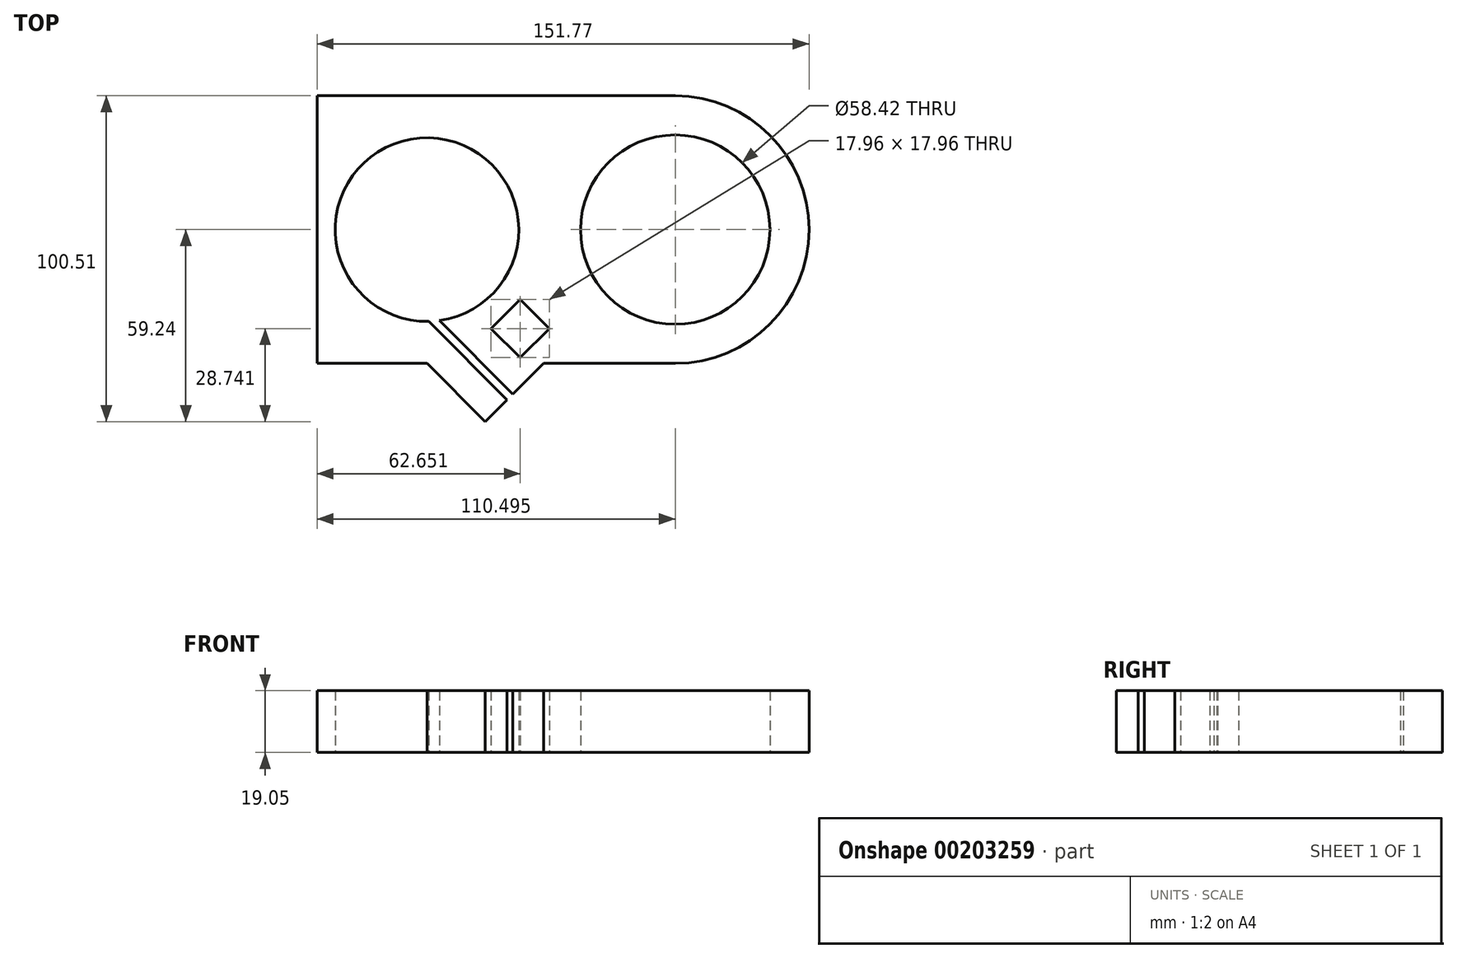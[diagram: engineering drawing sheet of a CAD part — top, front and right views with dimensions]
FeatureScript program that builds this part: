
annotation { "Feature Type Name" : "Feature", "Feature Type Description" : "" }
export const myFeature = defineFeature(function(context is Context, id is Id, definition is map)
    precondition{}
    {
        {
            var Q0;
            Q0=qCreatedBy(makeId("Top.planeOp"),FACE);
            var sketch = newSketch(context, id + "F0", { "sketchPlane" : qUnion([Q0])});
            skLineSegment(sketch, "E0.bottom", {"start": v(55.24, 41.28) * mm, "end": v(-55.25, 41.28) * mm});
            skLineSegment(sketch, "E0.top", {"start": v(55.24, -41.27) * mm, "end": v(14.59, -41.27) * mm});
            skLineSegment(sketch, "E0.right", {"start": v(-55.25, 41.28) * mm, "end": v(-55.25, -41.27) * mm});
            skPoint(sketch, "E0.middle", {"position": v(0, 0) * mm});
            skArc(sketch, "E1", {"start": v(-17.49, -28.06) * mm, "mid": v(-23.52, 28.24) * mm, "end": v(-20.82, -28.32) * mm});
            skArc(sketch, "E2", {"start": v(84.43, 1.27) * mm, "mid": v(26.03, 0) * mm, "end": v(84.43, -1.27) * mm});
            skArc(sketch, "E3", {"start": v(55.24, 41.28) * mm, "mid": v(80.33, 32.78) * mm, "end": v(95.08, 10.8) * mm});
            skArc(sketch, "E4.trimOffspring", {"start": v(95.08, -10.8) * mm, "mid": v(80.33, -32.78) * mm, "end": v(55.24, -41.28) * mm});
            skLineSegment(sketch, "E5", {"start": v(-21.34, -41.27) * mm, "end": v(-3.38, -59.24) * mm});
            skLineSegment(sketch, "E6", {"start": v(-3.38, -59.24) * mm, "end": v(3.36, -52.5) * mm});
            skLineSegment(sketch, "E7", {"start": v(3.36, -52.5) * mm, "end": v(-20.82, -28.32) * mm});
            skLineSegment(sketch, "E8", {"start": v(5.16, -50.7) * mm, "end": v(-17.49, -28.06) * mm});
            skLineSegment(sketch, "E9.trimOffspring", {"start": v(-7.87, -41.27) * mm, "end": v(-55.25, -41.27) * mm});
            skLineSegment(sketch, "E10", {"start": v(-4.27, -41.27) * mm, "end": v(5.16, -50.7) * mm});
            skPoint(sketch, "E11", {"position": v(-12.36, -50.26) * mm});
            skLineSegment(sketch, "E12", {"start": v(7.4, -39.48) * mm, "end": v(16.38, -30.5) * mm});
            skLineSegment(sketch, "E13", {"start": v(16.38, -30.5) * mm, "end": v(7.4, -21.52) * mm});
            skLineSegment(sketch, "E14", {"start": v(7.4, -21.52) * mm, "end": v(-1.58, -30.5) * mm});
            skLineSegment(sketch, "E15", {"start": v(5.16, -50.7) * mm, "end": v(14.59, -41.27) * mm});
            skLineSegment(sketch, "E16.trimOffspring", {"start": v(-2.93, -41.27) * mm, "end": v(-4.27, -41.27) * mm});
            skLineSegment(sketch, "E17", {"start": v(-1.58, -30.5) * mm, "end": v(7.4, -39.48) * mm});
            skLineSegment(sketch, "E18", {"start": v(-12.36, -50.26) * mm, "end": v(15.69, -22.21) * mm, "construction": true});
            skPoint(sketch, "E19", {"position": v(2.91, -34.99) * mm});
            skArc(sketch, "E20", {"start": v(84.43, 1.27) * mm, "mid": v(84.45, 0) * mm, "end": v(84.43, -1.27) * mm});
            skArc(sketch, "E21", {"start": v(95.08, 10.8) * mm, "mid": v(96.52, 0) * mm, "end": v(95.08, -10.8) * mm});
            skSolve(sketch);
        }
        {
            var Q0;
            Q0=makeQuery(id+"F0.imprint","IMPRINT",FACE,{"disambiguationData":[TD([[makeQuery(id+"F0.imprint","IMPRINT",EDGE,{"derivedFrom":sQuery(id+"F0.wireOp",EDGE,"E0.bottom")}),1.0]])]});
            var Q1;
            {var subQ0=sQuery(id+"F0.wireOp",EDGE,"E5");Q1=makeQuery(id+"F0.imprint","IMPRINT",FACE,{"disambiguationData":[TD([[makeQuery(id+"F0.imprint","IMPRINT",EDGE,{"derivedFrom":subQ0}),1.0]])]});}
            extrude(context, id + "F1", {"entities" : qUnion([Q0, Q1]), "depth" : 19.05 * mm});
        }
    });
